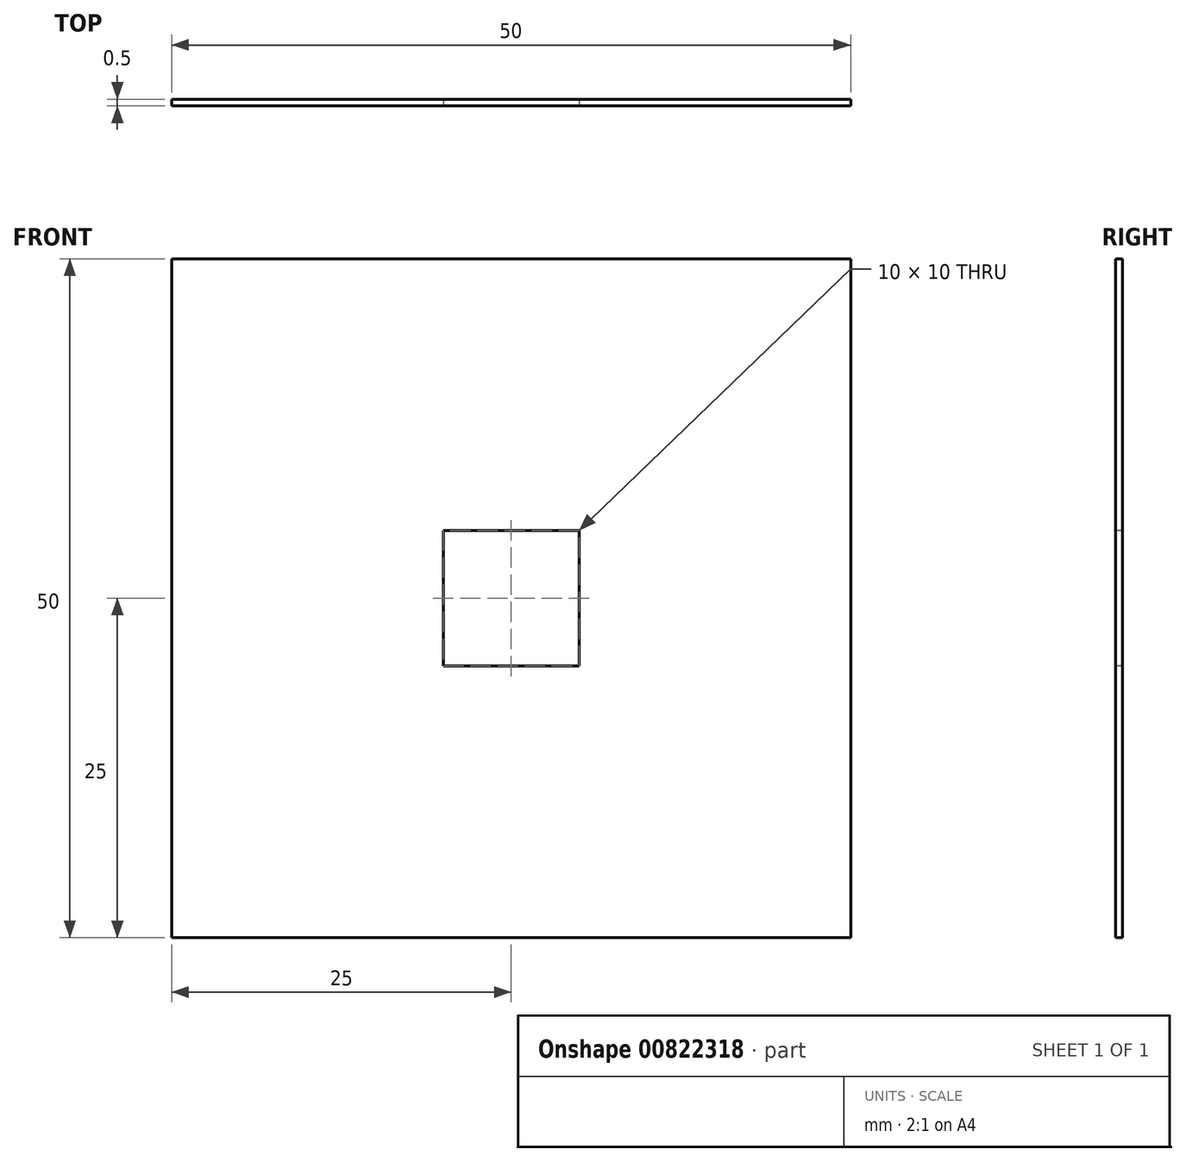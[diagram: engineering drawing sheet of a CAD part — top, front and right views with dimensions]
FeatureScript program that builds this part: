
annotation { "Feature Type Name" : "Feature", "Feature Type Description" : "" }
export const myFeature = defineFeature(function(context is Context, id is Id, definition is map)
    precondition{}
    {
        {
            var Q0;
            Q0=qCreatedBy(makeId("Front.planeOp"),FACE);
            var sketch = newSketch(context, id + "F0", { "sketchPlane" : qUnion([Q0])});
            skLineSegment(sketch, "E0.bottom", {"start": v(-25, 25) * mm, "end": v(25, 25) * mm});
            skLineSegment(sketch, "E0.top", {"start": v(-25, -25) * mm, "end": v(25, -25) * mm});
            skLineSegment(sketch, "E0.left", {"start": v(-25, 25) * mm, "end": v(-25, -25) * mm});
            skLineSegment(sketch, "E0.right", {"start": v(25, 25) * mm, "end": v(25, -25) * mm});
            skPoint(sketch, "E0.middle", {"position": v(0, 0) * mm});
            skSolve(sketch);
        }
        {
            var Q0;
            Q0 = qSketchRegion(id + "F0", true);
            extrude(context, id + "F1", {"entities" : qUnion([Q0]), "depth" : .5 * mm, "offsetDistance" : 25 * mm});
        }
        {
            var Q0;
            Q0=makeQuery(id+"F1.opExtrude","CAP_FACE",FACE,{"disambiguationData":[OSD([sQuery(id+"F0.wireOp",EDGE,"E0.bottom"),sQuery(id+"F0.wireOp",EDGE,"E0.top"),sQuery(id+"F0.wireOp",EDGE,"E0.left"),sQuery(id+"F0.wireOp",EDGE,"E0.right")])],"isStart":false});
            var sketch = newSketch(context, id + "F2", { "sketchPlane" : qUnion([Q0])});
            skLineSegment(sketch, "E1.bottom", {"start": v(-5, 5) * mm, "end": v(5, 5) * mm});
            skLineSegment(sketch, "E1.top", {"start": v(-5, -5) * mm, "end": v(5, -5) * mm});
            skLineSegment(sketch, "E1.left", {"start": v(-5, 5) * mm, "end": v(-5, -5) * mm});
            skLineSegment(sketch, "E1.right", {"start": v(5, 5) * mm, "end": v(5, -5) * mm});
            skPoint(sketch, "E1.middle", {"position": v(0, 0) * mm});
            skSolve(sketch);
        }
        {
            var Q0;
            Q0 = qSketchRegion(id + "F2", true);
            extrude(context, id + "F3", {"entities" : qUnion([Q0]), "operationType" : NewBodyOperationType.REMOVE, "oppositeDirection" : true, "depth" : .5 * mm, "offsetDistance" : 25 * mm});
        }
    });
